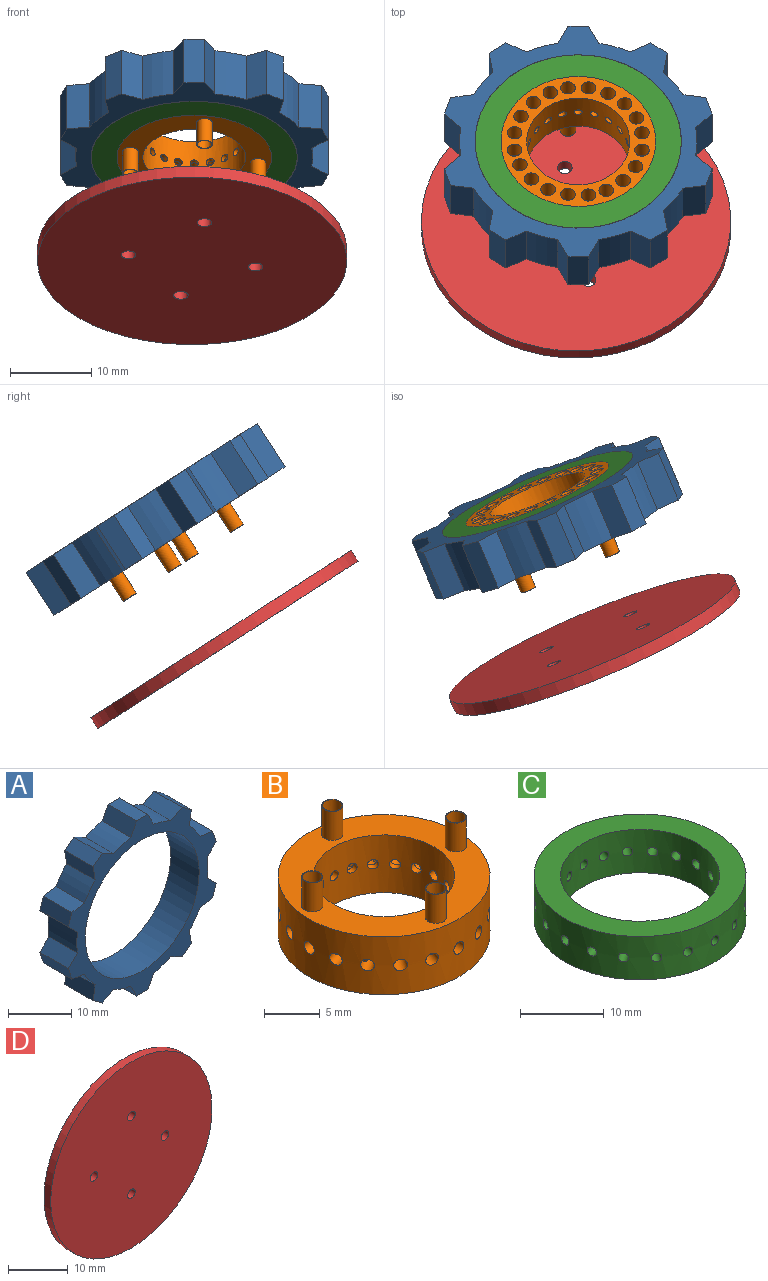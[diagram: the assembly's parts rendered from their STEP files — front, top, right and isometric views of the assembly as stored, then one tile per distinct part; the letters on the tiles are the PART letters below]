
ASSEMBLY  parts=4 mates=4
PART A: 43 faces, bbox 33x6.4x33.8 mm
  f0: plane 6.35x2.06mm, normal (0.59,0,-0.81), area 16.1mm2, adj f1,f39,f40,f41
  f1: plane 6.35x2.8mm, normal (0.99,0,0.16), area 18mm2, adj f0,f2,f40,f41
  f2: cylinder r=14.61mm len=6.35mm, axis (0,1,0), area 25.8mm2, adj f1,f3,f40,f41
  f3: plane 6.35x2.81mm, normal (0.15,0,-0.99), area 18mm2, adj f2,f4,f40,f41
  f4: plane 6.35x2.42mm, normal (0.95,0,-0.31), area 16.1mm2, adj f3,f5,f40,f41
  f5: plane 6.35x2.02mm, normal (0.7,0,0.71), area 18mm2, adj f4,f6,f40,f41
  f6: cylinder r=14.61mm len=6.35mm, axis (0,1,0), area 25.8mm2, adj f5,f7,f40,f41
  f7: plane 6.35x2.02mm, normal (0.7,0,-0.71), area 18mm2, adj f6,f8,f40,f41
  f8: plane 6.35x2.42mm, normal (0.95,0,0.31), area 16.1mm2, adj f7,f9,f40,f41
  f9: plane 6.35x2.81mm, normal (0.15,0,0.99), area 18mm2, adj f8,f10,f40,f41
  f10: cylinder r=14.61mm len=6.35mm, axis (0,1,0), area 25.8mm2, adj f9,f11,f40,f41
  f11: plane 6.35x2.8mm, normal (0.99,0,-0.16), area 18mm2, adj f10,f12,f40,f41
  f12: plane 6.35x2.06mm, normal (0.59,0,0.81), area 16.1mm2, adj f11,f13,f40,f41
  f13: plane 6.35x2.52mm, normal (-0.46,0,0.89), area 18mm2, adj f12,f14,f40,f41
  f14: cylinder r=14.61mm len=6.35mm, axis (0,1,0), area 25.8mm2, adj f13,f15,f40,f41
  f15: plane 6.35x2.54mm, normal (0.89,0,0.45), area 18mm2, adj f14,f16,f40,f41
  f16: plane 6.35x2.54mm, normal (0,0,1), area 16.1mm2, adj f15,f17,f40,f41
  f17: plane 6.35x2.54mm, normal (-0.89,0,0.45), area 18mm2, adj f16,f18,f40,f41
  f18: cylinder r=14.61mm len=6.35mm, axis (0,1,0), area 25.8mm2, adj f17,f19,f40,f41
  f19: plane 6.35x2.52mm, normal (0.46,0,0.89), area 18mm2, adj f18,f20,f40,f41
  f20: plane 6.35x2.06mm, normal (-0.59,0,0.81), area 16.1mm2, adj f19,f21,f40,f41
  f21: plane 6.35x2.8mm, normal (-0.99,0,-0.16), area 18mm2, adj f20,f22,f40,f41
  f22: cylinder r=14.61mm len=6.35mm, axis (0,1,0), area 25.8mm2, adj f21,f23,f40,f41
  f23: plane 6.35x2.81mm, normal (-0.15,0,0.99), area 18mm2, adj f22,f24,f40,f41
  f24: plane 6.35x2.42mm, normal (-0.95,0,0.31), area 16.1mm2, adj f23,f25,f40,f41
  f25: plane 6.35x2.02mm, normal (-0.7,0,-0.71), area 18mm2, adj f24,f26,f40,f41
  f26: cylinder r=14.61mm len=6.35mm, axis (0,1,0), area 25.8mm2, adj f25,f27,f40,f41
  f27: plane 6.35x2.02mm, normal (-0.7,0,0.71), area 18mm2, adj f26,f28,f40,f41
  f28: plane 6.35x2.42mm, normal (-0.95,0,-0.31), area 16.1mm2, adj f27,f29,f40,f41
  f29: plane 6.35x2.81mm, normal (-0.15,0,-0.99), area 18mm2, adj f28,f30,f40,f41
  f30: cylinder r=14.61mm len=6.35mm, axis (0,1,0), area 25.8mm2, adj f29,f31,f40,f41
  f31: plane 6.35x2.8mm, normal (-0.99,0,0.16), area 18mm2, adj f30,f32,f40,f41
  f32: plane 6.35x2.06mm, normal (-0.59,0,-0.81), area 16.1mm2, adj f31,f33,f40,f41
  f33: plane 6.35x2.52mm, normal (0.46,0,-0.89), area 18mm2, adj f32,f34,f40,f41
  f34: cylinder r=14.61mm len=6.35mm, axis (0,1,0), area 25.8mm2, adj f33,f35,f40,f41
  f35: plane 6.35x2.54mm, normal (-0.89,0,-0.45), area 18mm2, adj f34,f36,f40,f41
  f36: plane 6.35x2.54mm, normal (0,0,-1), area 16.1mm2, adj f35,f37,f40,f41
  f37: plane 6.35x2.54mm, normal (0.89,0,-0.45), area 18mm2, adj f36,f38,f40,f41
  f38: cylinder r=14.61mm len=6.35mm, axis (0,1,0), area 25.8mm2, adj f37,f39,f40,f41
  f39: plane 6.35x2.52mm, normal (-0.46,0,-0.89), area 18mm2, adj f0,f38,f40,f41
  f40: plane 33.85x32.97mm, normal (0,-1,0), area 252.6mm2, adj f0,f1,f2,f3,f4,f5,f6,f7
  f41: plane 33.85x32.97mm, normal (0,1,0), area 252.6mm2, adj f0,f1,f2,f3,f4,f5,f6,f7
  f42: cylinder r=12.7mm len=25.4mm, axis (0,1,0), area 506.7mm2, adj f40,f41
PART B: 108 faces, bbox 19.1x19.1x9.5 mm
  f0: cylinder r=9.53mm len=19.05mm, axis (0,0,-1), area 354.8mm2, adj f2,f3,f24,f26,f28,f30,f32,f34
  f1: cylinder r=6.35mm len=12.7mm, axis (0,0,-1), area 237.1mm2, adj f2,f3,f4,f5,f6,f7,f8,f9
  f2: plane 19.05x19.05mm, normal (0,0,1), area 146.9mm2, adj f0,f1,f64,f66,f68,f70
  f3: plane 19.05x19.05mm, normal (0,0,-1), area 108.7mm2, adj f0,f1,f72,f73,f74,f75,f76,f78
  f4: cylinder r=0.51mm len=1.02mm, axis (0,-1,0), area 2.1mm2, adj f1,f25
  f5: cylinder r=0.51mm len=1.17mm, axis (0.31,-0.95,0), area 2.1mm2, adj f1,f27
  f6: cylinder r=0.51mm len=1.21mm, axis (0.59,-0.81,0), area 2.1mm2, adj f1,f29
  f7: cylinder r=0.51mm len=1.21mm, axis (0.81,-0.59,0), area 2.1mm2, adj f1,f31
  f8: cylinder r=0.51mm len=1.17mm, axis (0.95,-0.31,0), area 2.1mm2, adj f1,f33
  f9: cylinder r=0.51mm len=1.02mm, axis (1,0,0), area 2.1mm2, adj f1,f35
  f10: cylinder r=0.51mm len=1.17mm, axis (0.95,0.31,0), area 2.1mm2, adj f1,f37
  f11: cylinder r=0.51mm len=1.21mm, axis (0.81,0.59,0), area 2.1mm2, adj f1,f39
  f12: cylinder r=0.51mm len=1.21mm, axis (0.59,0.81,0), area 2.1mm2, adj f1,f41
  f13: cylinder r=0.51mm len=1.17mm, axis (0.31,0.95,0), area 2.1mm2, adj f1,f43
  f14: cylinder r=0.51mm len=1.02mm, axis (0,1,0), area 2.1mm2, adj f1,f45
  f15: cylinder r=0.51mm len=1.17mm, axis (-0.31,0.95,0), area 2.1mm2, adj f1,f47
  f16: cylinder r=0.51mm len=1.21mm, axis (-0.59,0.81,0), area 2.1mm2, adj f1,f49
  f17: cylinder r=0.51mm len=1.21mm, axis (-0.81,0.59,0), area 2.1mm2, adj f1,f51
  f18: cylinder r=0.51mm len=1.17mm, axis (-0.95,0.31,0), area 2.1mm2, adj f1,f53
  f19: cylinder r=0.51mm len=1.02mm, axis (-1,0,0), area 2.1mm2, adj f1,f55
  f20: cylinder r=0.51mm len=1.17mm, axis (-0.95,-0.31,0), area 2.1mm2, adj f1,f57
  f21: cylinder r=0.51mm len=1.21mm, axis (-0.81,-0.59,0), area 2.1mm2, adj f1,f59
  f22: cylinder r=0.51mm len=1.21mm, axis (-0.59,-0.81,0), area 2.1mm2, adj f1,f61
  f23: cylinder r=0.51mm len=1.17mm, axis (-0.31,-0.95,0), area 2.1mm2, adj f1,f63
  f24: cylinder r=0.64mm len=2.54mm, axis (0,1,0), area 7.8mm2, adj f0,f25,f75,f106
  f25: plane 1.27x1.27mm, normal (0,1,0), area 0.5mm2, adj f4,f24
  f26: cylinder r=0.64mm len=2.81mm, axis (-0.31,0.95,0), area 7.8mm2, adj f0,f27,f104,f106
  f27: plane 1.27x1.21mm, normal (-0.31,0.95,0), area 0.5mm2, adj f5,f26
  f28: cylinder r=0.64mm len=2.8mm, axis (-0.59,0.81,0), area 7.8mm2, adj f0,f29,f102,f104
  f29: plane 1.27x1.03mm, normal (-0.59,0.81,0), area 0.5mm2, adj f6,f28
  f30: cylinder r=0.64mm len=2.8mm, axis (-0.81,0.59,0), area 7.8mm2, adj f0,f31,f100,f102
  f31: plane 1.27x1.03mm, normal (-0.81,0.59,0), area 0.5mm2, adj f7,f30
  f32: cylinder r=0.64mm len=2.81mm, axis (-0.95,0.31,0), area 6.5mm2, adj f0,f33,f72,f100
  f33: plane 1.27x1.21mm, normal (-0.95,0.31,0), area 0.5mm2, adj f8,f32
  f34: cylinder r=0.64mm len=2.54mm, axis (-1,0,0), area 7.8mm2, adj f0,f35,f72,f98
  f35: plane 1.27x1.27mm, normal (-1,0,0), area 0.5mm2, adj f9,f34
  f36: cylinder r=0.64mm len=2.81mm, axis (-0.95,-0.31,0), area 7.8mm2, adj f0,f37,f96,f98
  f37: plane 1.27x1.21mm, normal (-0.95,-0.31,0), area 0.5mm2, adj f10,f36
  f38: cylinder r=0.64mm len=2.8mm, axis (-0.81,-0.59,0), area 7.8mm2, adj f0,f39,f94,f96
  f39: plane 1.27x1.03mm, normal (-0.81,-0.59,0), area 0.5mm2, adj f11,f38
  f40: cylinder r=0.64mm len=2.8mm, axis (-0.59,-0.81,0), area 7.8mm2, adj f0,f41,f92,f94
  f41: plane 1.27x1.03mm, normal (-0.59,-0.81,0), area 0.5mm2, adj f12,f40
  f42: cylinder r=0.64mm len=2.81mm, axis (-0.31,-0.95,0), area 6.6mm2, adj f0,f43,f73,f92
  f43: plane 1.27x1.21mm, normal (-0.31,-0.95,0), area 0.5mm2, adj f13,f42
  f44: cylinder r=0.64mm len=2.54mm, axis (0,-1,0), area 7.8mm2, adj f0,f45,f73,f90
  f45: plane 1.27x1.27mm, normal (0,-1,0), area 0.5mm2, adj f14,f44
  f46: cylinder r=0.64mm len=2.81mm, axis (0.31,-0.95,0), area 7.8mm2, adj f0,f47,f88,f90
  f47: plane 1.27x1.21mm, normal (0.31,-0.95,0), area 0.5mm2, adj f15,f46
  f48: cylinder r=0.64mm len=2.8mm, axis (0.59,-0.81,0), area 7.8mm2, adj f0,f49,f86,f88
  f49: plane 1.27x1.03mm, normal (0.59,-0.81,0), area 0.5mm2, adj f16,f48
  f50: cylinder r=0.64mm len=2.8mm, axis (0.81,-0.59,0), area 7.8mm2, adj f0,f51,f84,f86
  f51: plane 1.27x1.03mm, normal (0.81,-0.59,0), area 0.5mm2, adj f17,f50
  f52: cylinder r=0.64mm len=2.81mm, axis (0.95,-0.31,0), area 6.6mm2, adj f0,f53,f74,f84
  f53: plane 1.27x1.21mm, normal (0.95,-0.31,0), area 0.5mm2, adj f18,f52
  f54: cylinder r=0.64mm len=2.54mm, axis (1,0,0), area 7.8mm2, adj f0,f55,f74,f82
  f55: plane 1.27x1.27mm, normal (1,0,0), area 0.5mm2, adj f19,f54
  f56: cylinder r=0.64mm len=2.81mm, axis (0.95,0.31,0), area 7.8mm2, adj f0,f57,f80,f82
  f57: plane 1.27x1.21mm, normal (0.95,0.31,0), area 0.5mm2, adj f20,f56
  f58: cylinder r=0.64mm len=2.8mm, axis (0.81,0.59,0), area 7.8mm2, adj f0,f59,f78,f80
  f59: plane 1.27x1.03mm, normal (0.81,0.59,0), area 0.5mm2, adj f21,f58
  f60: cylinder r=0.64mm len=2.8mm, axis (0.59,0.81,0), area 7.8mm2, adj f0,f61,f76,f78
  f61: plane 1.27x1.03mm, normal (0.59,0.81,0), area 0.5mm2, adj f22,f60
  f62: cylinder r=0.64mm len=2.81mm, axis (0.31,0.95,0), area 6.6mm2, adj f0,f63,f75,f76
  f63: plane 1.27x1.21mm, normal (0.31,0.95,0), area 0.5mm2, adj f23,f62
  f64: cylinder r=0.95mm len=3.18mm, axis (0,0,-1), area 19mm2, adj f2,f65
  f65: plane 1.91x1.91mm, normal (0,0,1), area 0.4mm2, adj f64,f75
  f66: cylinder r=0.95mm len=3.18mm, axis (0,0,-1), area 19mm2, adj f2,f67
  f67: plane 1.91x1.91mm, normal (0,0,1), area 0.4mm2, adj f66,f74
  f68: cylinder r=0.95mm len=3.18mm, axis (0,0,-1), area 19mm2, adj f2,f69
  f69: plane 1.91x1.91mm, normal (0,0,1), area 0.4mm2, adj f68,f73
  f70: cylinder r=0.95mm len=3.18mm, axis (0,0,-1), area 19mm2, adj f2,f71
  f71: plane 1.91x1.91mm, normal (0,0,1), area 0.4mm2, adj f70,f72
  f72: cylinder r=0.89mm len=9.53mm, axis (0,0,-1), area 50.7mm2, adj f3,f32,f34,f71
  f73: cylinder r=0.89mm len=9.53mm, axis (0,0,-1), area 50.7mm2, adj f3,f42,f44,f69
  f74: cylinder r=0.89mm len=9.53mm, axis (0,0,-1), area 50.7mm2, adj f3,f52,f54,f67
  f75: cylinder r=0.89mm len=9.53mm, axis (0,0,-1), area 50.7mm2, adj f3,f24,f62,f65
  f76: cylinder r=0.89mm len=5.08mm, axis (0,0,-1), area 26mm2, adj f3,f60,f62,f77
  f77: plane 1.78x1.78mm, normal (0,0,-1), area 2.5mm2, adj f76
  f78: cylinder r=0.89mm len=5.08mm, axis (0,0,-1), area 25.9mm2, adj f3,f58,f60,f79
  f79: plane 1.78x1.78mm, normal (0,0,-1), area 2.5mm2, adj f78
  f80: cylinder r=0.89mm len=5.08mm, axis (0,0,-1), area 25.9mm2, adj f3,f56,f58,f81
  f81: plane 1.78x1.78mm, normal (0,0,-1), area 2.5mm2, adj f80
  f82: cylinder r=0.89mm len=5.08mm, axis (0,0,-1), area 25.9mm2, adj f3,f54,f56,f83
  f83: plane 1.78x1.78mm, normal (0,0,-1), area 2.5mm2, adj f82
  f84: cylinder r=0.89mm len=5.08mm, axis (0,0,-1), area 26mm2, adj f3,f50,f52,f85
  f85: plane 1.78x1.78mm, normal (0,0,-1), area 2.5mm2, adj f84
  f86: cylinder r=0.89mm len=5.08mm, axis (0,0,-1), area 26mm2, adj f3,f48,f50,f87
  f87: plane 1.78x1.78mm, normal (0,0,-1), area 2.5mm2, adj f86
  f88: cylinder r=0.89mm len=5.08mm, axis (0,0,-1), area 25.9mm2, adj f3,f46,f48,f89
  f89: plane 1.78x1.78mm, normal (0,0,-1), area 2.5mm2, adj f88
  f90: cylinder r=0.89mm len=5.08mm, axis (0,0,-1), area 25.9mm2, adj f3,f44,f46,f91
  f91: plane 1.78x1.78mm, normal (0,0,-1), area 2.5mm2, adj f90
  f92: cylinder r=0.89mm len=5.08mm, axis (0,0,-1), area 26mm2, adj f3,f40,f42,f93
  f93: plane 1.78x1.78mm, normal (0,0,-1), area 2.5mm2, adj f92
  f94: cylinder r=0.89mm len=5.08mm, axis (0,0,-1), area 26mm2, adj f3,f38,f40,f95
  f95: plane 1.78x1.78mm, normal (0,0,-1), area 2.5mm2, adj f94
  f96: cylinder r=0.89mm len=5.08mm, axis (0,0,-1), area 25.9mm2, adj f3,f36,f38,f97
  f97: plane 1.78x1.78mm, normal (0,0,-1), area 2.5mm2, adj f96
  f98: cylinder r=0.89mm len=5.08mm, axis (0,0,-1), area 25.9mm2, adj f3,f34,f36,f99
  f99: plane 1.78x1.78mm, normal (0,0,-1), area 2.5mm2, adj f98
  f100: cylinder r=0.89mm len=5.08mm, axis (0,0,-1), area 26mm2, adj f3,f30,f32,f101
  f101: plane 1.78x1.78mm, normal (0,0,-1), area 2.5mm2, adj f100
  f102: cylinder r=0.89mm len=5.08mm, axis (0,0,-1), area 26mm2, adj f3,f28,f30,f103
  f103: plane 1.78x1.78mm, normal (0,0,-1), area 2.5mm2, adj f102
  f104: cylinder r=0.89mm len=5.08mm, axis (0,0,-1), area 25.9mm2, adj f3,f26,f28,f105
  f105: plane 1.78x1.78mm, normal (0,0,-1), area 2.5mm2, adj f104
  f106: cylinder r=0.89mm len=5.08mm, axis (0,0,-1), area 25.8mm2, adj f3,f24,f26,f107
  f107: plane 1.78x1.78mm, normal (0,0,-1), area 2.5mm2, adj f106
PART C: 24 faces, bbox 25.4x25.4x6.4 mm
  f0: cylinder r=9.53mm len=19.05mm, axis (0,0,-1), area 354.6mm2, adj f2,f3,f4,f5,f6,f7,f8,f9
  f1: cylinder r=12.7mm len=25.4mm, axis (0,0,-1), area 481.2mm2, adj f2,f3,f4,f5,f6,f7,f8,f9
  f2: plane 25.4x25.4mm, normal (0,0,1), area 221.7mm2, adj f0,f1
  f3: plane 25.4x25.4mm, normal (0,0,-1), area 221.7mm2, adj f0,f1
  f4: cylinder r=0.64mm len=3.2mm, axis (0,-1,0), area 12.7mm2, adj f0,f1
  f5: cylinder r=0.64mm len=3.43mm, axis (0.31,-0.95,0), area 12.7mm2, adj f0,f1
  f6: cylinder r=0.64mm len=3.33mm, axis (0.59,-0.81,0), area 12.7mm2, adj f0,f1
  f7: cylinder r=0.64mm len=3.33mm, axis (0.81,-0.59,0), area 12.7mm2, adj f0,f1
  f8: cylinder r=0.64mm len=3.43mm, axis (0.95,-0.31,0), area 12.7mm2, adj f0,f1
  f9: cylinder r=0.64mm len=3.2mm, axis (1,0,0), area 12.7mm2, adj f0,f1
  f10: cylinder r=0.64mm len=3.43mm, axis (0.95,0.31,0), area 12.7mm2, adj f0,f1
  f11: cylinder r=0.64mm len=3.33mm, axis (0.81,0.59,0), area 12.7mm2, adj f0,f1
  f12: cylinder r=0.64mm len=3.33mm, axis (0.59,0.81,0), area 12.7mm2, adj f0,f1
  f13: cylinder r=0.64mm len=3.43mm, axis (0.31,0.95,0), area 12.7mm2, adj f0,f1
  f14: cylinder r=0.64mm len=3.2mm, axis (0,1,0), area 12.7mm2, adj f0,f1
  f15: cylinder r=0.64mm len=3.43mm, axis (-0.31,0.95,0), area 12.7mm2, adj f0,f1
  f16: cylinder r=0.64mm len=3.33mm, axis (-0.59,0.81,0), area 12.7mm2, adj f0,f1
  f17: cylinder r=0.64mm len=3.33mm, axis (-0.81,0.59,0), area 12.7mm2, adj f0,f1
  f18: cylinder r=0.64mm len=3.43mm, axis (-0.95,0.31,0), area 12.7mm2, adj f0,f1
  f19: cylinder r=0.64mm len=3.2mm, axis (-1,0,0), area 12.7mm2, adj f0,f1
  f20: cylinder r=0.64mm len=3.43mm, axis (-0.95,-0.31,0), area 12.7mm2, adj f0,f1
  f21: cylinder r=0.64mm len=3.33mm, axis (-0.81,-0.59,0), area 12.7mm2, adj f0,f1
  f22: cylinder r=0.64mm len=3.33mm, axis (-0.59,-0.81,0), area 12.7mm2, adj f0,f1
  f23: cylinder r=0.64mm len=3.43mm, axis (-0.31,-0.95,0), area 12.7mm2, adj f0,f1
PART D: 7 faces, bbox 38.1x1.6x38.1 mm
  f0: cylinder r=19.05mm len=38.1mm, axis (0,1,0), area 190mm2, adj f1,f2
  f1: plane 38.1x38.1mm, normal (0,-1,0), area 1130.2mm2, adj f0,f3,f4,f5,f6
  f2: plane 38.1x38.1mm, normal (0,1,0), area 1130.2mm2, adj f0,f3,f4,f5,f6
  f3: cylinder r=0.89mm len=1.78mm, axis (0,1,0), area 8.9mm2, adj f1,f2
  f4: cylinder r=0.89mm len=1.78mm, axis (0,1,0), area 8.9mm2, adj f1,f2
  f5: cylinder r=0.89mm len=1.78mm, axis (0,1,0), area 8.9mm2, adj f1,f2
  f6: cylinder r=0.89mm len=1.78mm, axis (0,1,0), area 8.9mm2, adj f1,f2
PLACE A rot(axis=(1,0,0),57.2deg) t=(27.73,-21.88,32.94)mm
PLACE B rot(axis=(1,0,0),147.2deg) t=(27.73,-21.88,32.94)mm
PLACE C rot(axis=(1,0,0),147.2deg) t=(27.73,-21.88,32.94)mm
PLACE D rot(axis=(-0.59,-0.39,0.71),144.1deg) t=(27.46,-30.79,17.5)mm
MATE cylindrical D.f6 <-> B.f64  axis (0,-0.54,-0.84) through (29,-38.11,22.21)mm
MATE planar A.f34 <-> C.f1  axis (0,0.54,0.84) through (27.73,-20.16,35.61)mm
MATE revolute C.f0 <-> B.f1  axis (0,0.54,0.84) through (27.73,-21.88,32.94)mm
MATE cylindrical A.f42 <-> C.f1  axis (0,0.54,0.84) through (27.73,-23.6,30.27)mm
